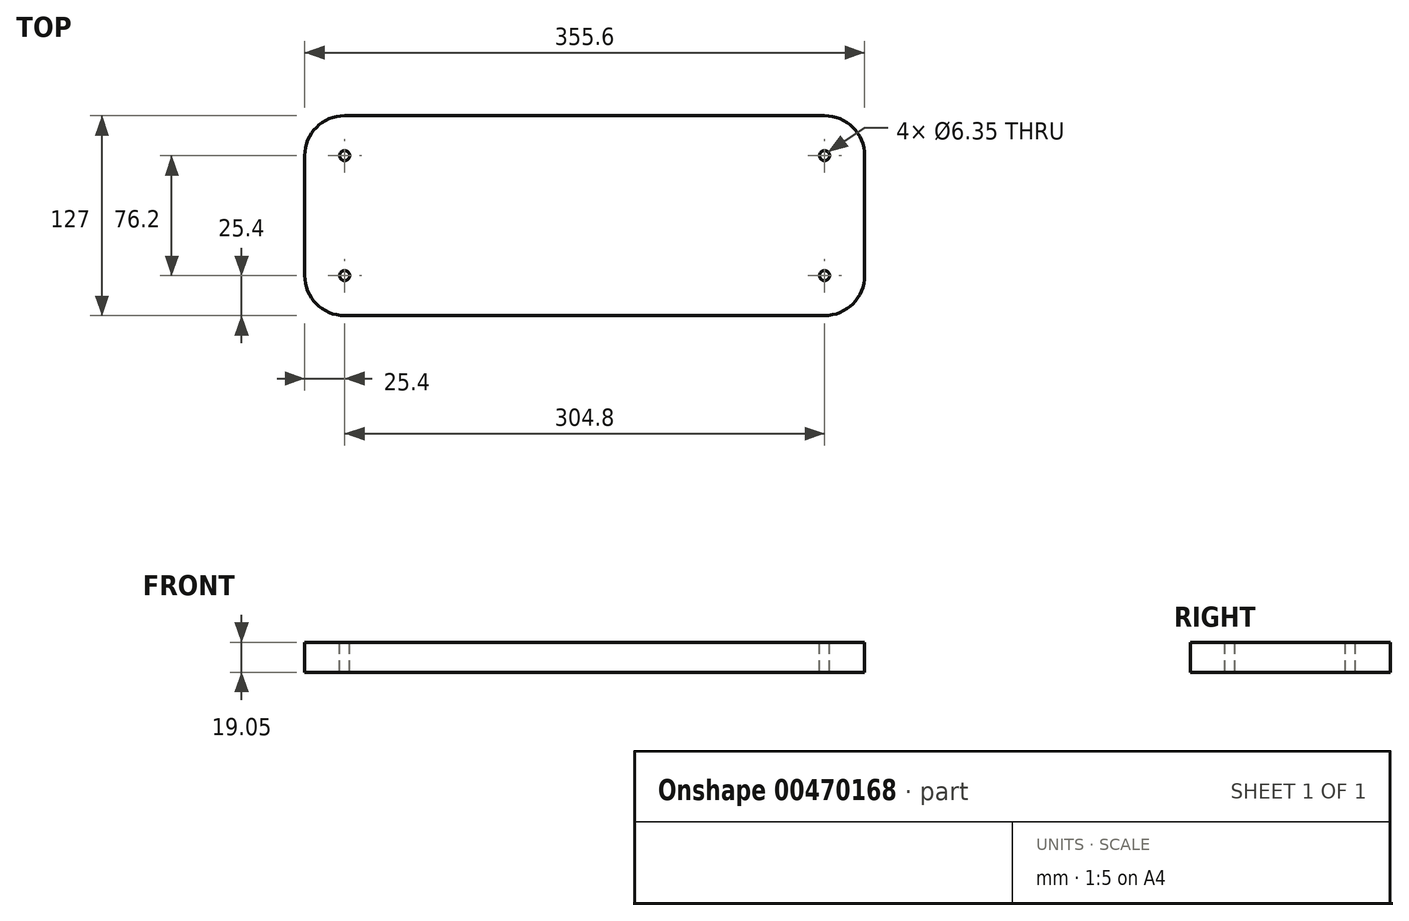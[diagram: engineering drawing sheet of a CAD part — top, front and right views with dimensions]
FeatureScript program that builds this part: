
annotation { "Feature Type Name" : "Feature", "Feature Type Description" : "" }
export const myFeature = defineFeature(function(context is Context, id is Id, definition is map)
    precondition{}
    {
        {
            var Q0;
            Q0=qCreatedBy(makeId("Top.planeOp"),FACE);
            var sketch = newSketch(context, id + "F0", { "sketchPlane" : qUnion([Q0])});
            skLineSegment(sketch, "E0.bottom", {"start": v(177.8, 63.5) * mm, "end": v(-177.8, 63.5) * mm});
            skLineSegment(sketch, "E0.top", {"start": v(177.8, -63.5) * mm, "end": v(-177.8, -63.5) * mm});
            skLineSegment(sketch, "E0.left", {"start": v(177.8, 63.5) * mm, "end": v(177.8, -63.5) * mm});
            skLineSegment(sketch, "E0.right", {"start": v(-177.8, 63.5) * mm, "end": v(-177.8, -63.5) * mm});
            skPoint(sketch, "E0.middle", {"position": v(0, 0) * mm});
            skSolve(sketch);
        }
        {
            var Q0;
            Q0=makeQuery(id+"F0.imprint","IMPRINT",FACE,{"disambiguationData":[TD([[makeQuery(id+"F0.imprint","IMPRINT",EDGE,{"derivedFrom":sQuery(id+"F0.wireOp",EDGE,"E0.bottom")}),1.0]])]});
            extrude(context, id + "F1", {"entities" : qUnion([Q0]), "depth" : 19.05 * mm});
        }
        {
            var Q0;
            Q0=makeQuery(id+"F1.opExtrude","SWEPT_EDGE",EDGE,{"disambiguationData":[OSD([sQuery(id+"F0.wireOp",EDGE,"E0.bottom"),sQuery(id+"F0.wireOp",EDGE,"E0.right")])]});
            var Q1;
            Q1=makeQuery(id+"F1.opExtrude","SWEPT_EDGE",EDGE,{"disambiguationData":[OSD([sQuery(id+"F0.wireOp",EDGE,"E0.top"),sQuery(id+"F0.wireOp",EDGE,"E0.right")])]});
            var Q2;
            Q2=makeQuery(id+"F1.opExtrude","SWEPT_EDGE",EDGE,{"disambiguationData":[OSD([sQuery(id+"F0.wireOp",EDGE,"E0.top"),sQuery(id+"F0.wireOp",EDGE,"E0.left")])]});
            var Q3;
            Q3=makeQuery(id+"F1.opExtrude","SWEPT_EDGE",EDGE,{"disambiguationData":[OSD([sQuery(id+"F0.wireOp",EDGE,"E0.bottom"),sQuery(id+"F0.wireOp",EDGE,"E0.left")])]});
            fillet(context, id + "F2", {"entities" : qUnion([Q0, Q1, Q2, Q3]), "radius" : 25.4 * mm, "tangentPropagation" : true, "allowEdgeOverflow" : false});
        }
        {
            var Q0;
            Q0=makeQuery(id+"F1.opExtrude","CAP_FACE",FACE,{"disambiguationData":[OSD([sQuery(id+"F0.wireOp",EDGE,"E0.bottom"),sQuery(id+"F0.wireOp",EDGE,"E0.top"),sQuery(id+"F0.wireOp",EDGE,"E0.left"),sQuery(id+"F0.wireOp",EDGE,"E0.right")])],"isStart":false});
            var sketch = newSketch(context, id + "F3", { "sketchPlane" : qUnion([Q0])});
            skCircle(sketch, "E1", {"center": v(-152.4, 38.1) * mm, "radius": 3.18 * mm});
            skCircle(sketch, "E2", {"center": v(-152.4, -38.1) * mm, "radius": 3.18 * mm});
            skCircle(sketch, "E3", {"center": v(152.4, 38.1) * mm, "radius": 3.18 * mm});
            skCircle(sketch, "E4", {"center": v(152.4, -38.1) * mm, "radius": 3.18 * mm});
            skSolve(sketch);
        }
        {
            var Q0;
            Q0 = qSketchRegion(id + "F3", true);
            extrude(context, id + "F4", {"entities" : qUnion([Q0]), "operationType" : NewBodyOperationType.REMOVE, "endBound" : BoundingType.THROUGH_ALL, "oppositeDirection" : true, "depth" : 25.4 * mm});
        }
    });
